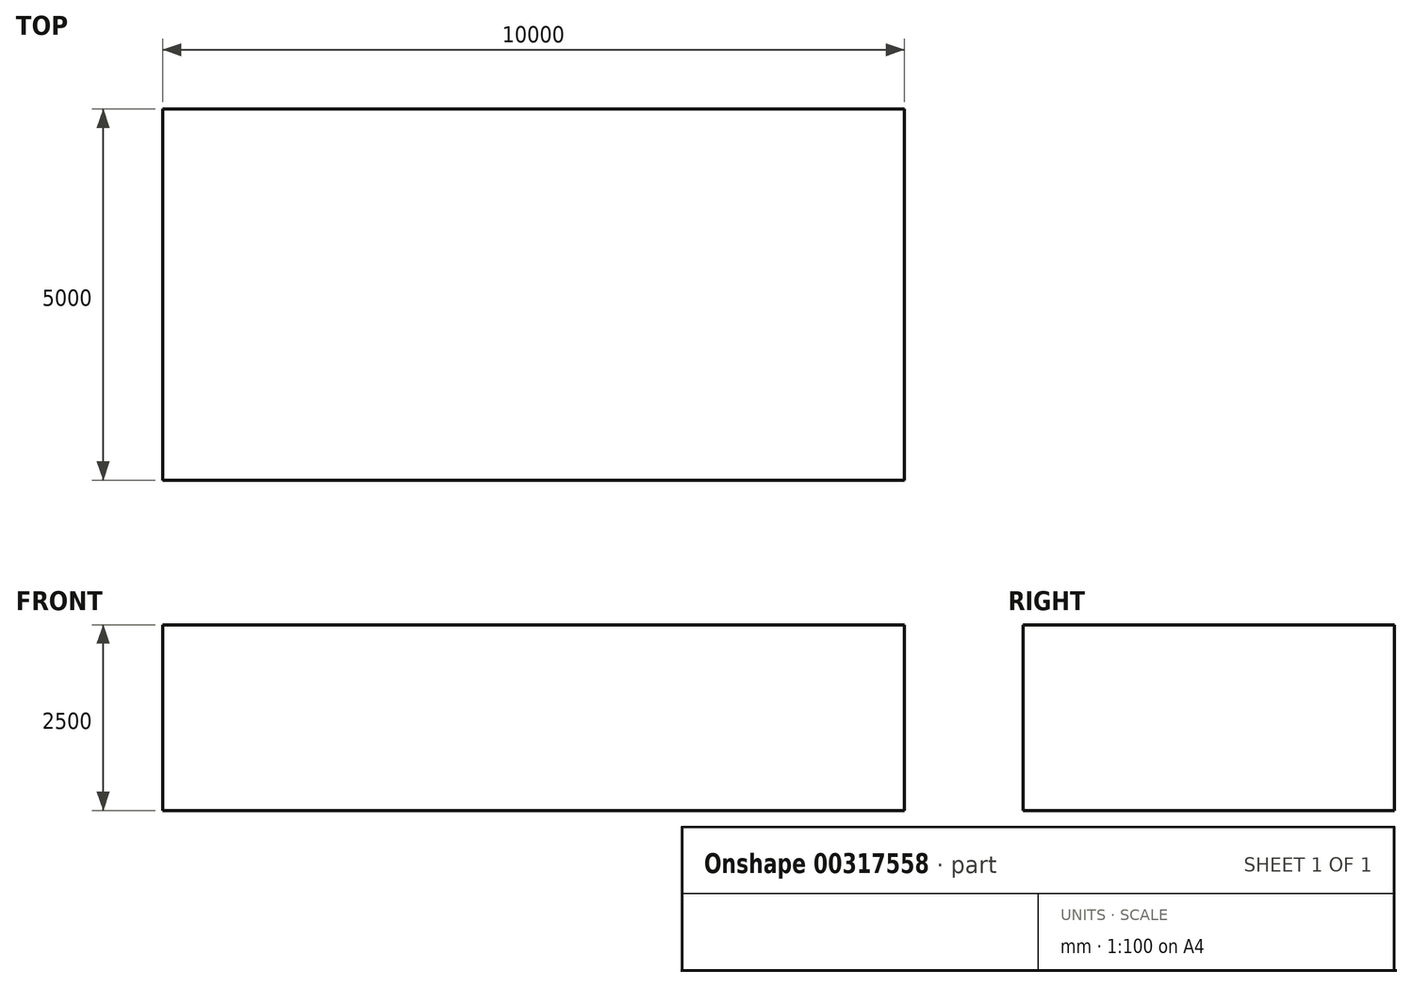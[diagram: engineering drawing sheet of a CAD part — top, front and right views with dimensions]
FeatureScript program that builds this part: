
annotation { "Feature Type Name" : "Feature", "Feature Type Description" : "" }
export const myFeature = defineFeature(function(context is Context, id is Id, definition is map)
    precondition{}
    {
        {
            var Q0;
            Q0=qCreatedBy(makeId("Front.planeOp"),FACE);
            var sketch = newSketch(context, id + "F0", { "sketchPlane" : qUnion([Q0])});
            skLineSegment(sketch, "E0.bottom", {"start": v(0, 0) * mm, "end": v(-10000, 0) * mm});
            skLineSegment(sketch, "E0.top", {"start": v(0, 2500) * mm, "end": v(-10000, 2500) * mm});
            skLineSegment(sketch, "E0.left", {"start": v(0, 0) * mm, "end": v(0, 2500) * mm});
            skLineSegment(sketch, "E0.right", {"start": v(-10000, 0) * mm, "end": v(-10000, 2500) * mm});
            skSolve(sketch);
        }
        {
            var Q0;
            Q0 = qSketchRegion(id + "F0", true);
            extrude(context, id + "F1", {"entities" : qUnion([Q0]), "depth" : 5000 * mm});
        }
    });
